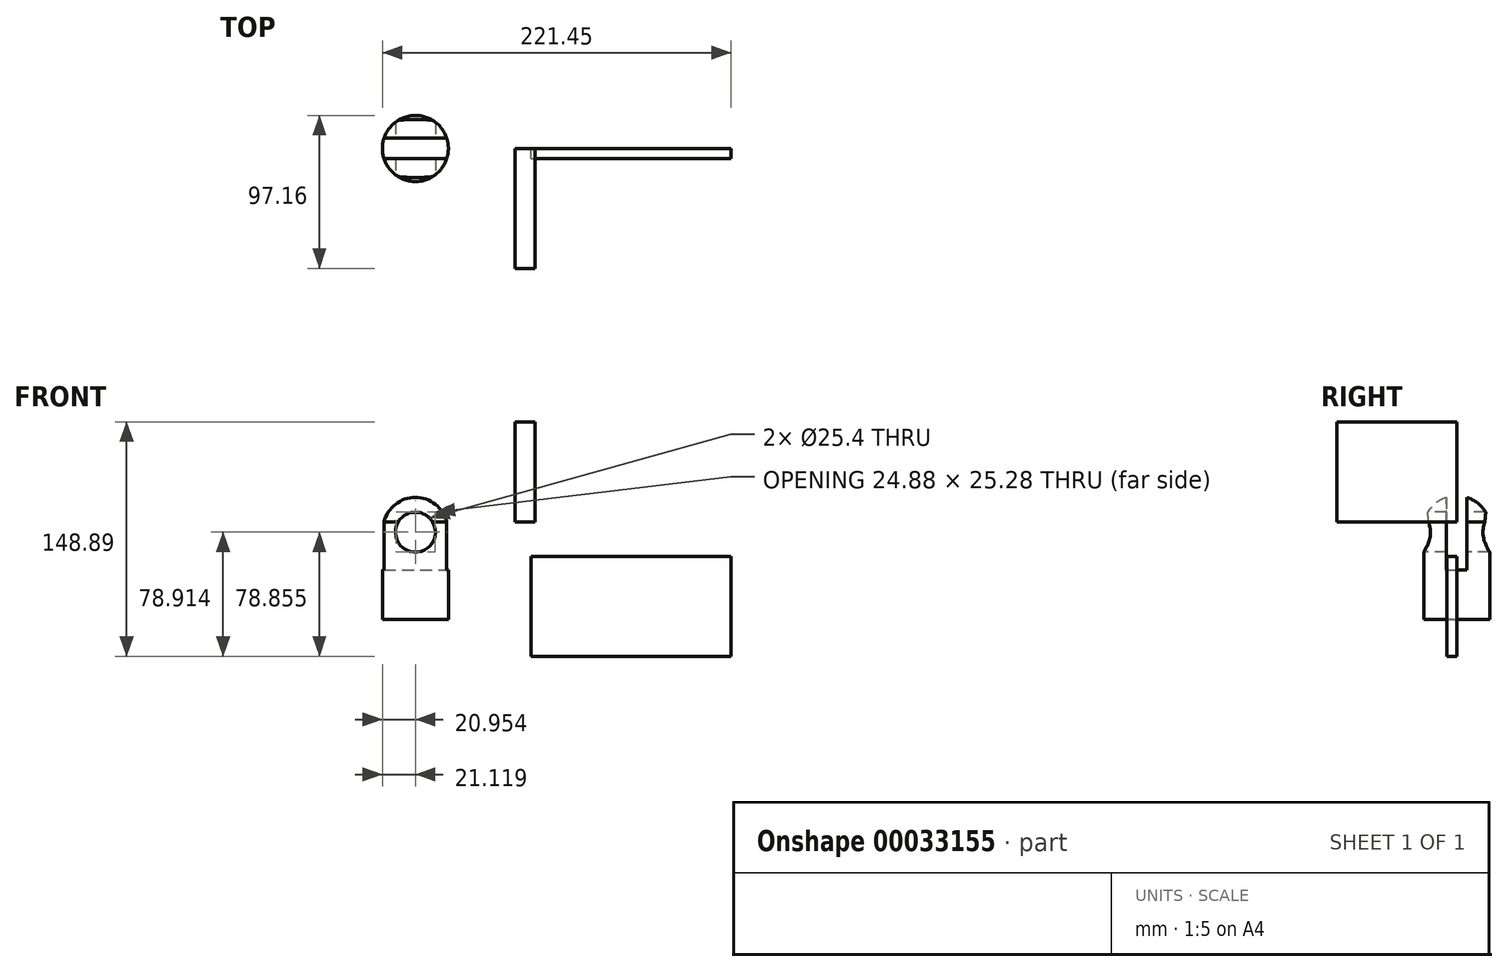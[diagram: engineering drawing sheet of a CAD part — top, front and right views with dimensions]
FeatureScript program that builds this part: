
annotation { "Feature Type Name" : "Feature", "Feature Type Description" : "" }
export const myFeature = defineFeature(function(context is Context, id is Id, definition is map)
    precondition{}
    {
        {
            var Q0;
            Q0=qCreatedBy(makeId("Front.planeOp"),FACE);
            var sketch = newSketch(context, id + "F0", { "sketchPlane" : qUnion([Q0])});
            skLineSegment(sketch, "E0.bottom", {"start": v(-39.6, 8.69) * mm, "end": v(87.4, 8.69) * mm});
            skLineSegment(sketch, "E0.top", {"start": v(-39.6, -54.81) * mm, "end": v(87.4, -54.81) * mm});
            skLineSegment(sketch, "E0.left", {"start": v(-39.6, 8.69) * mm, "end": v(-39.6, -54.81) * mm});
            skLineSegment(sketch, "E0.right", {"start": v(87.4, 8.69) * mm, "end": v(87.4, -54.81) * mm});
            skLineSegment(sketch, "E1.bottom", {"start": v(-39.6, 8.69) * mm, "end": v(-32.83, 8.69) * mm});
            skLineSegment(sketch, "E1.top", {"start": v(-39.6, -54.81) * mm, "end": v(-32.83, -54.81) * mm});
            skLineSegment(sketch, "E2.bottom", {"start": v(87.4, 8.69) * mm, "end": v(17.97, 8.69) * mm});
            skLineSegment(sketch, "E2.top", {"start": v(87.4, -54.81) * mm, "end": v(17.97, -54.81) * mm});
            skLineSegment(sketch, "E3.bottom", {"start": v(-49.65, 94.08) * mm, "end": v(-36.95, 94.08) * mm});
            skLineSegment(sketch, "E3.top", {"start": v(-49.65, 30.58) * mm, "end": v(-36.95, 30.58) * mm});
            skLineSegment(sketch, "E3.left", {"start": v(-49.65, 94.08) * mm, "end": v(-49.65, 30.58) * mm});
            skLineSegment(sketch, "E3.right", {"start": v(-36.95, 94.08) * mm, "end": v(-36.95, 30.58) * mm});
            skPoint(sketch, "E4.centerSnap0", {"position": v(23.9, 8.69) * mm});
            skLineSegment(sketch, "E5", {"start": v(-39.6, -23.06) * mm, "end": v(87.4, -23.06) * mm, "construction": true});
            skCircle(sketch, "E6", {"center": v(-113.09, 24.05) * mm, "radius": 12.7 * mm});
            skLineSegment(sketch, "E7.top", {"start": v(-134.04, -31.3) * mm, "end": v(-113.09, -31.3) * mm});
            skLineSegment(sketch, "E7.left", {"start": v(-134.04, 30.5) * mm, "end": v(-134.04, -31.3) * mm});
            skLineSegment(sketch, "E7.right", {"start": v(-113.09, 47.15) * mm, "end": v(-113.09, 36.75) * mm});
            skArc(sketch, "E8", {"start": v(-113.09, 47.15) * mm, "mid": v(-126.47, 42.48) * mm, "end": v(-134.04, 30.5) * mm});
            skLineSegment(sketch, "E9.trimOffspring", {"start": v(-113.09, 25.64) * mm, "end": v(-113.09, 24.05) * mm});
            skLineSegment(sketch, "E10.trimOffspring", {"start": v(-113.09, 11.35) * mm, "end": v(-113.09, -31.3) * mm});
            skSolve(sketch);
        }
        {
            var Q0;
            Q0=makeQuery(id+"F0.imprint","IMPRINT",FACE,{"disambiguationData":[TD([[makeQuery(id+"F0.imprint","IMPRINT",EDGE,{"derivedFrom":sQuery(id+"F0.wireOp",EDGE,"E0.bottom")}),-1.0]])]});
            var Q1;
            Q1=makeQuery(id+"F0.imprint","IMPRINT",FACE,{"disambiguationData":[TD([[makeQuery(id+"F0.imprint","IMPRINT",EDGE,{"derivedFrom":sQuery(id+"F0.wireOp",EDGE,"E4")}),1.0]])]});
            extrude(context, id + "F1", {"entities" : qUnion([Q0, Q1]), "depth" : 6.35 * mm});
        }
        {
            var Q0;
            Q0=makeQuery(id+"F0.imprint","IMPRINT",FACE,{"disambiguationData":[TD([[makeQuery(id+"F0.imprint","IMPRINT",EDGE,{"derivedFrom":sQuery(id+"F0.wireOp",EDGE,"E3.bottom")}),-1.0]])]});
            extrude(context, id + "F2", {"entities" : qUnion([Q0]), "depth" : 76.2 * mm});
        }
        {
            var Q0;
            Q0=makeQuery(id+"F0.imprint","IMPRINT",FACE,{"disambiguationData":[TD([[makeQuery(id+"F0.imprint","IMPRINT",EDGE,{"derivedFrom":sQuery(id+"F0.wireOp",EDGE,"E7.top")}),1.0]])]});
            var Q1;
            {var subQ0=sQuery(id+"F0.wireOp",EDGE,"E6");var subQ2=makeQuery(id+"F0.imprint","INTERSECT",VERTEX,{"derivedFrom":[subQ0,sQuery(id+"F0.wireOp",EDGE,"E7.right")]});Q1=makeQuery(id+"F0.imprint","IMPRINT",FACE,{"disambiguationData":[TD([[makeQuery(id+"F0.imprint","IMPRINT",EDGE,{"disambiguationData":[TD([[subQ2,-1.0]])],"derivedFrom":subQ0}),1.0]])]});}
            var Q2;
            Q2=sQuery(id+"F0.wireOp",EDGE,"E10.trimOffspring");
            revolve(context, id + "F3", {"entities" : qUnion([Q0, Q1]), "axis" : qUnion([Q2]), "revolveType" : RevolveType.FULL});
        }
        {
            var Q0;
            {var subQ0=sQuery(id+"F0.wireOp",EDGE,"E6");var subQ2=makeQuery(id+"F0.imprint","INTERSECT",VERTEX,{"derivedFrom":[subQ0,sQuery(id+"F0.wireOp",EDGE,"E7.right")]});Q0=makeQuery(id+"F0.imprint","IMPRINT",FACE,{"disambiguationData":[TD([[makeQuery(id+"F0.imprint","IMPRINT",EDGE,{"disambiguationData":[TD([[subQ2,-1.0]])],"derivedFrom":subQ0}),1.0]])]});}
            extrude(context, id + "F4", {"entities" : qUnion([Q0]), "operationType" : NewBodyOperationType.REMOVE, "endBound" : BoundingType.THROUGH_ALL, "oppositeDirection" : true, "depth" : 25.4 * mm});
        }
        {
            var Q0;
            {var subQ0=sQuery(id+"F0.wireOp",EDGE,"E6");var subQ2=makeQuery(id+"F0.imprint","INTERSECT",VERTEX,{"derivedFrom":[subQ0,sQuery(id+"F0.wireOp",EDGE,"E7.right")]});Q0=makeQuery(id+"F0.imprint","IMPRINT",FACE,{"disambiguationData":[TD([[makeQuery(id+"F0.imprint","IMPRINT",EDGE,{"disambiguationData":[TD([[subQ2,-1.0]])],"derivedFrom":subQ0}),1.0]])]});}
            extrude(context, id + "F5", {"entities" : qUnion([Q0]), "operationType" : NewBodyOperationType.REMOVE, "depth" : 25.4 * mm});
        }
        {
            var Q0;
            Q0=qCreatedBy(makeId("Top.planeOp"),FACE);
            var sketch = newSketch(context, id + "F6", { "sketchPlane" : qUnion([Q0])});
            skLineSegment(sketch, "E11.bottom", {"start": v(-134.04, 6.48) * mm, "end": v(-92.13, 6.48) * mm});
            skLineSegment(sketch, "E11.top", {"start": v(-134.04, -6.48) * mm, "end": v(-92.13, -6.48) * mm});
            skLineSegment(sketch, "E11.left", {"start": v(-134.04, 6.48) * mm, "end": v(-134.04, -6.48) * mm});
            skLineSegment(sketch, "E11.right", {"start": v(-92.13, 6.48) * mm, "end": v(-92.13, -6.48) * mm});
            skSolve(sketch);
        }
        {
            var Q0;
            Q0 = qSketchRegion(id + "F6", true);
            extrude(context, id + "F7", {"entities" : qUnion([Q0]), "operationType" : NewBodyOperationType.REMOVE, "depth" : 78.4 * mm});
        }
    });
